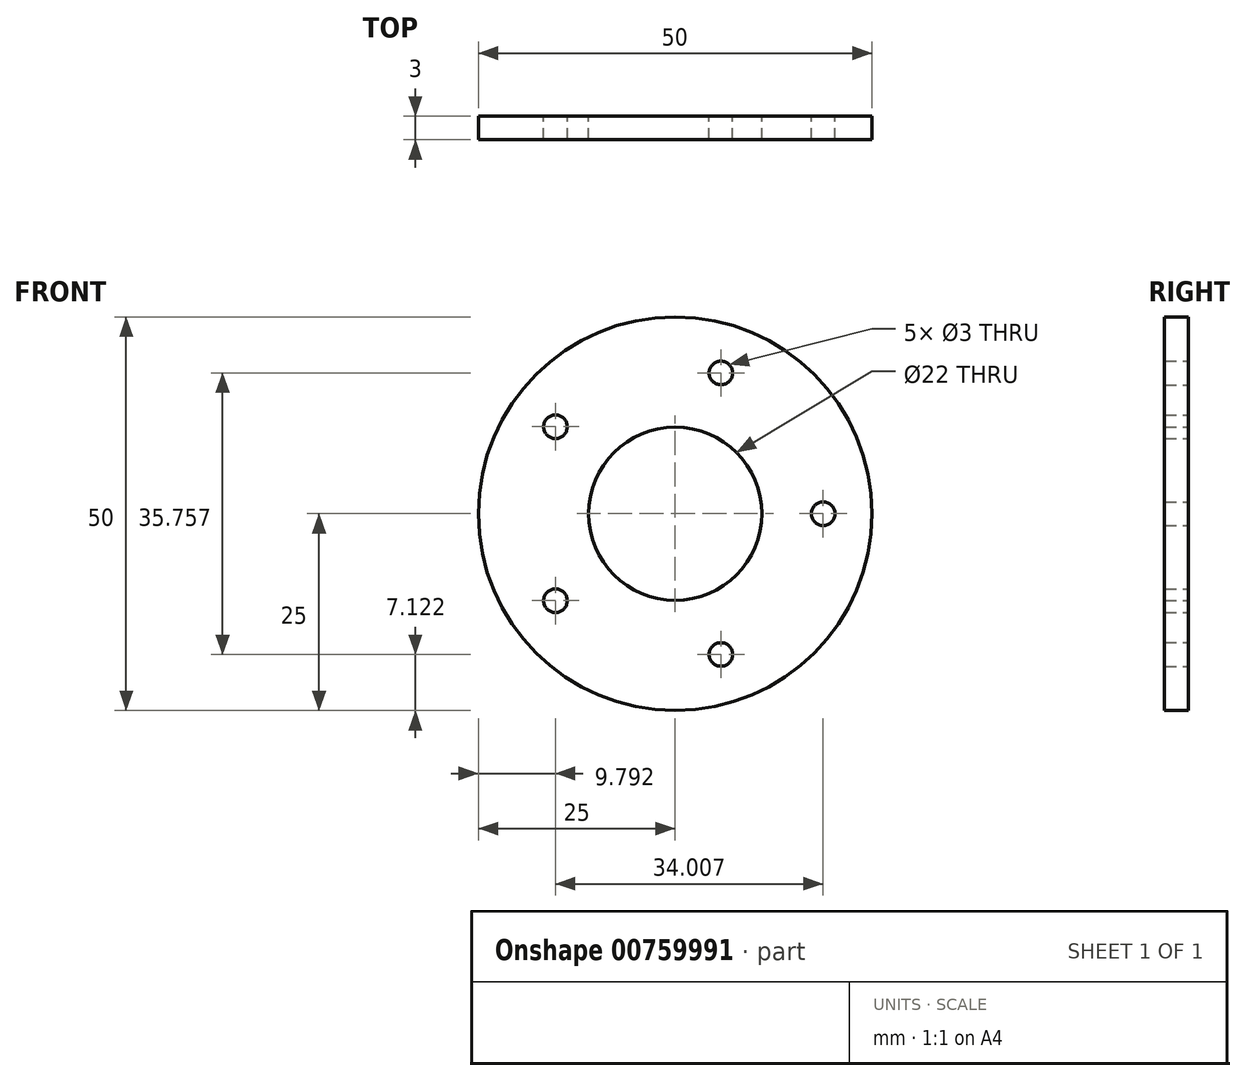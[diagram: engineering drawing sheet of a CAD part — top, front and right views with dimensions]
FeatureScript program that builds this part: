
annotation { "Feature Type Name" : "Feature", "Feature Type Description" : "" }
export const myFeature = defineFeature(function(context is Context, id is Id, definition is map)
    precondition{}
    {
        {
            var Q0;
            Q0=qCreatedBy(makeId("Front.planeOp"),FACE);
            var sketch = newSketch(context, id + "F0", { "sketchPlane" : qUnion([Q0])});
            skArc(sketch, "E0", {"start": v(-3.4, 10.46) * mm, "mid": v(-8.9, 6.47) * mm, "end": v(-11, 0) * mm});
            skArc(sketch, "E1", {"start": v(-7.73, 23.78) * mm, "mid": v(-20.23, 14.7) * mm, "end": v(-25, 0) * mm});
            skCircle(sketch, "E2", {"center": v(-15.2, 11.05) * mm, "radius": 1.5 * mm});
            skArc(sketch, "E3.1.0", {"start": v(-25, 0) * mm, "mid": v(-20.23, -14.7) * mm, "end": v(-7.73, -23.78) * mm});
            skArc(sketch, "E3.1.1", {"start": v(-11, 0) * mm, "mid": v(-8.9, -6.47) * mm, "end": v(-3.4, -10.46) * mm});
            skCircle(sketch, "E3.1.2", {"center": v(-15.2, -11.05) * mm, "radius": 1.5 * mm});
            skArc(sketch, "E3.2.0", {"start": v(-7.73, -23.78) * mm, "mid": v(7.73, -23.78) * mm, "end": v(20.23, -14.7) * mm});
            skArc(sketch, "E3.2.1", {"start": v(-3.4, -10.46) * mm, "mid": v(3.4, -10.46) * mm, "end": v(8.9, -6.47) * mm});
            skCircle(sketch, "E3.2.2", {"center": v(5.8, -17.88) * mm, "radius": 1.5 * mm});
            skArc(sketch, "E4.3.3.0", {"start": v(20.23, -14.7) * mm, "mid": v(25, 0) * mm, "end": v(20.23, 14.7) * mm});
            skArc(sketch, "E4.4.3.0", {"start": v(8.9, -6.47) * mm, "mid": v(11, 0) * mm, "end": v(8.9, 6.47) * mm});
            skCircle(sketch, "E4.8.3.0", {"center": v(18.8, 0) * mm, "radius": 1.5 * mm});
            skArc(sketch, "E4.3.4.0", {"start": v(20.23, 14.7) * mm, "mid": v(7.73, 23.78) * mm, "end": v(-7.73, 23.78) * mm});
            skArc(sketch, "E4.4.4.0", {"start": v(8.9, 6.47) * mm, "mid": v(3.4, 10.46) * mm, "end": v(-3.4, 10.46) * mm});
            skCircle(sketch, "E4.8.4.0", {"center": v(5.8, 17.88) * mm, "radius": 1.5 * mm});
            skSolve(sketch);
        }
        {
            var Q0;
            Q0 = qSketchRegion(id + "F0", true);
            extrude(context, id + "F1", {"entities" : qUnion([Q0]), "depth" : 3 * mm, "offsetDistance" : 25 * mm});
        }
    });
